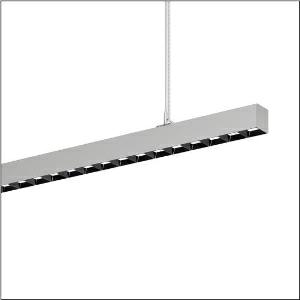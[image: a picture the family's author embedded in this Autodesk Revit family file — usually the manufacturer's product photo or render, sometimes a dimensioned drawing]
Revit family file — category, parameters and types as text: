
# Revit family: silica_r__21_51mx31tat7s_2b6e
name_source: partatom
category: Lighting Fixtures
units: mm (PartAtom-declared; Revit-internal decimal feet)

## family parameters
Cut with Voids When Loaded = No
Host = Face
Light Source = No
Part Type = Normal
Room Calculation Point = No
Round Connector Dimension = Use Diameter
Shared = No

## types (1)
- --- (1 x LED, 6220 lm, 53.5 W, 6500K)
    Apparent Load = 54 VA
    CIE Flux Codes = 85 99 100 60 100
    Color Rendering = 80
    Color Temperature = 6500K
    Default Elevation = 1800 mm
    Description = Silica® 21, office luminaire, primary light control with darklight reflector, of PMMA, black, CAT 2 (L<= 3000cd/m²), light emission: direct/indirect distribution, primary light characteristic: symmetric, installation type: suspended mounting, LED, rated luminous flux: 6.220lm, luminous efficacy: 111lm/W, light colour: 8tw, colour temperature: 2700..6500K, control gear: ECG DALI, with terminal, 3+2-pole, max. 2.5mm², mains connection: 220..240V, AC, 50/60Hz, rated input power: 56.2W, luminaire housing, of aluminium, metallic grey (RAL 9006), length: 1.204mm, width: 53mm, height: 53mm, protection rating (complete): IP20, insulation class (complete): insulation class I (protective earthing), certification: CE, permissible operating ambient temperature: 0..+35°C, standard: EN 50419, packaging unit: 1 piece
    Height = 53 mm
    Lamp = 1 x LED
    Lamp Light Flux = 6220 lm
    Lamp Power = 53.5 W
    Lamp count = 1
    Length = 1204 mm
    Luminous efficacy = 116 lm/W
    Manufacturer = Siteco
    ModVariant = No
    Model = 51MX31TAT7S
    Mounting Place = Ceiling
    Mounting Type = Pendant
    Number of Poles = 1
    OnlyDefault = Yes
    Power Factor = 1
    Product Name = Silica® 21
    Product group = office luminaire | ceiling pendant
    ProductGroupID = 902
    Protection Class = Protection class I
    Protection Degree = IP 20
    RLX_Detail_Level = 1
    RLX_Emergency_Light_Flux = 0 lm
    RLX_Emergency_Type = 0
    RLX_Emergency_Type_DB = No
    RlxData = <blob elided: 41289 chars, md5=156c1e97>
    Socket = socket
    Standby Power = 0 W
    System Light Flux = 6220 lm
    System Power = 54 W
    Type Comments = individual setting
    Type Image = l_1297751.jpg
    URL = http://relux.com
    VarID = @adj_071197
    Voltage = 0 V
    Weight = 0.00 kg
    Width = 53 mm

## geometry (parser evidence)
native form markers: Blend x4, Sweep x11
no freeform markers — native parametric forms only
